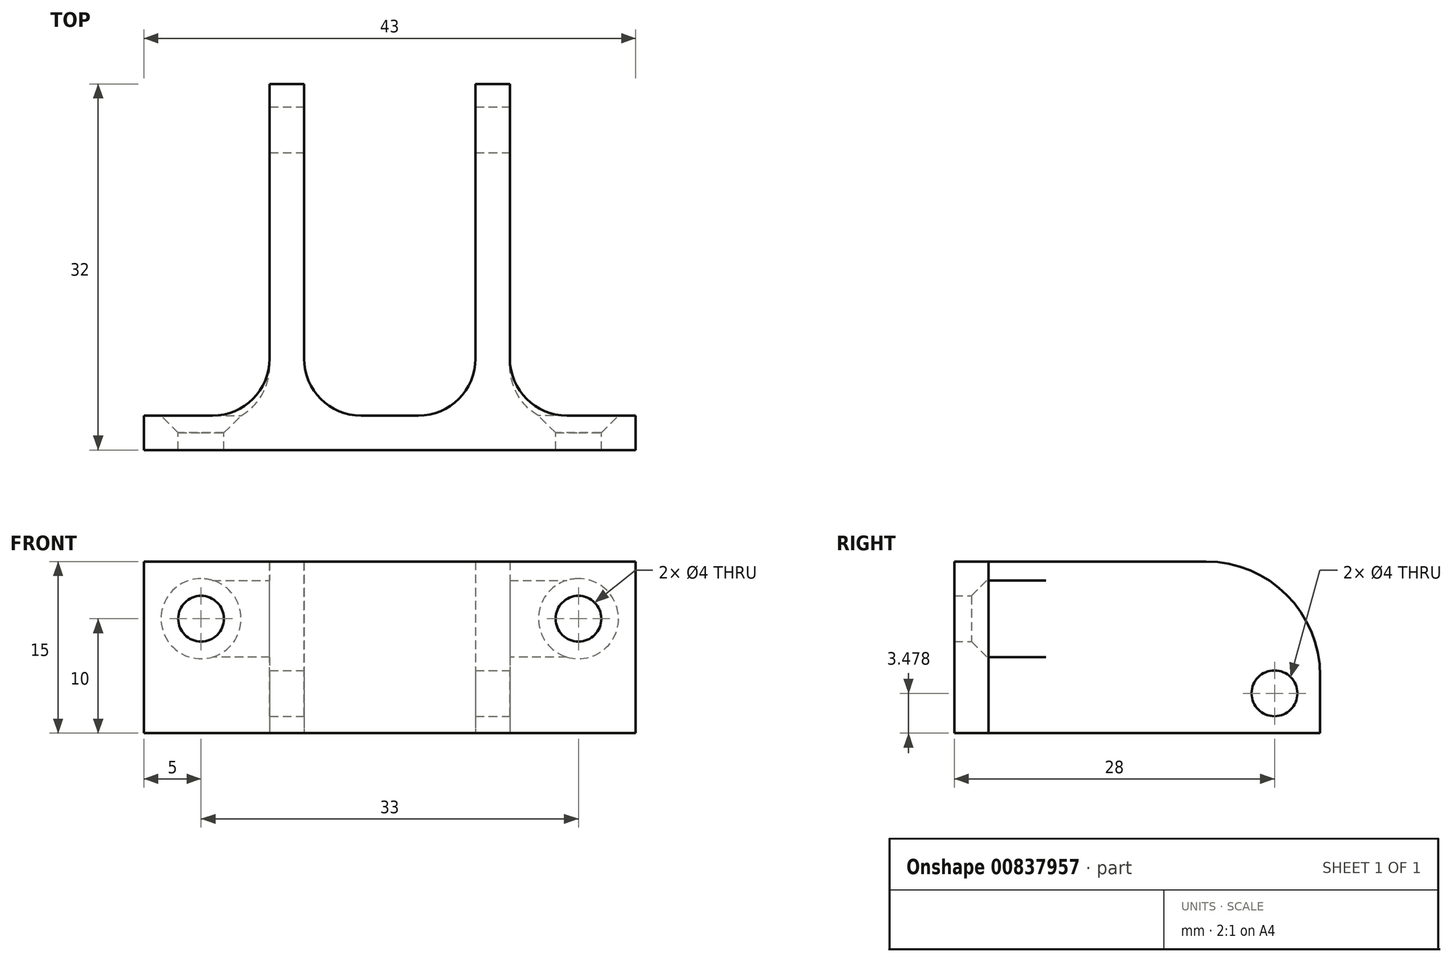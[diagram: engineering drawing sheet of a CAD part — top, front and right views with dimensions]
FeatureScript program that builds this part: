
annotation { "Feature Type Name" : "Feature", "Feature Type Description" : "" }
export const myFeature = defineFeature(function(context is Context, id is Id, definition is map)
    precondition{}
    {
        {
            var Q0;
            Q0=qCreatedBy(makeId("Top.planeOp"),FACE);
            var sketch = newSketch(context, id + "F0", { "sketchPlane" : qUnion([Q0])});
            skLineSegment(sketch, "E0", {"start": v(0, 29) * mm, "end": v(0, 0) * mm});
            skLineSegment(sketch, "E1", {"start": v(0, 0) * mm, "end": v(15, 0) * mm});
            skLineSegment(sketch, "E2", {"start": v(15, 0) * mm, "end": v(15, 29) * mm});
            skLineSegment(sketch, "E3", {"start": v(0, 0) * mm, "end": v(-14, 0) * mm});
            skLineSegment(sketch, "E4", {"start": v(15, 0) * mm, "end": v(29, 0) * mm});
            skLineSegment(sketch, "E5.0", {"start": v(18, -3) * mm, "end": v(18, 29) * mm});
            skLineSegment(sketch, "E5.1", {"start": v(-3, -3) * mm, "end": v(18, -3) * mm});
            skLineSegment(sketch, "E5.2", {"start": v(-3, 29) * mm, "end": v(-3, -3) * mm});
            skLineSegment(sketch, "E6", {"start": v(-3, -3) * mm, "end": v(-14, -3) * mm});
            skLineSegment(sketch, "E7", {"start": v(-14, -3) * mm, "end": v(-14, 0) * mm});
            skLineSegment(sketch, "E8", {"start": v(18, -3) * mm, "end": v(29, -3) * mm});
            skLineSegment(sketch, "E9", {"start": v(29, -3) * mm, "end": v(29, 0) * mm});
            skLineSegment(sketch, "E10", {"start": v(15, 29) * mm, "end": v(18, 29) * mm});
            skLineSegment(sketch, "E11", {"start": v(0, 29) * mm, "end": v(-3, 29) * mm});
            skSolve(sketch);
        }
        {
            var Q0;
            Q0 = qSketchRegion(id + "F0", true);
            extrude(context, id + "F1", {"entities" : qUnion([Q0]), "depth" : 15 * mm, "offsetDistance" : 25 * mm});
        }
        {
            var Q0;
            Q0=makeQuery(id+"F1.opExtrude","SWEPT_FACE",FACE,{"disambiguationData":[OSD([sQuery(id+"F0.wireOp",EDGE,"E5.0")])]});
            var sketch = newSketch(context, id + "F2", { "sketchPlane" : qUnion([Q0])});
            skLineSegment(sketch, "E12", {"start": v(25, 15) * mm, "end": v(25, 0) * mm, "construction": true});
            skLineSegment(sketch, "E13", {"start": v(28, 15) * mm, "end": v(28, 0) * mm, "construction": true});
            skCircle(sketch, "E14", {"center": v(25, 3.48) * mm, "radius": 2 * mm});
            skSolve(sketch);
        }
        {
            var Q0;
            Q0=makeQuery(id+"F2.imprint","IMPRINT",FACE,{"disambiguationData":[TD([[makeQuery(id+"F2.imprint","IMPRINT",EDGE,{"derivedFrom":sQuery(id+"F2.wireOp",EDGE,"E14")}),1.0]])]});
            var Q1;
            Q1=sQuery(id+"F2.wireOp",EDGE,"E14");
            extrude(context, id + "F3", {"entities" : qUnion([Q0]), "operationType" : NewBodyOperationType.REMOVE, "surfaceEntities" : qUnion([Q1]), "oppositeDirection" : true, "depth" : 25 * mm, "offsetDistance" : 25 * mm});
        }
        {
            var Q0;
            Q0=makeQuery(id+"F1.opExtrude","SWEPT_FACE",FACE,{"disambiguationData":[OSD([sQuery(id+"F0.wireOp",EDGE,"E4")])]});
            var sketch = newSketch(context, id + "F4", { "sketchPlane" : qUnion([Q0])});
            skLineSegment(sketch, "E15", {"start": v(-7.5, 0) * mm, "end": v(-7.5, 15.31) * mm, "construction": true});
            skLineSegment(sketch, "E16", {"start": v(13.84, 10) * mm, "end": v(-29, 10) * mm, "construction": true});
            skLineSegment(sketch, "E17", {"start": v(9, 0) * mm, "end": v(9, 15.42) * mm, "construction": true});
            skPoint(sketch, "E18", {"position": v(9, 10) * mm});
            skPoint(sketch, "E19", {"position": v(16.74, 5.7) * mm});
            skPoint(sketch, "E20.MirrorP", {"position": v(-24, 10) * mm});
            skSolve(sketch);
        }
        {
            var Q0;
            Q0=sQuery(id+"F4.wireOp",VERTEX,"E18");
            var Q1;
            Q1=sQuery(id+"F4.wireOp",VERTEX,"E20.MirrorP");
            var Q2;
            Q2=makeQuery(id+"F1.opExtrude","SWEPT_BODY",BODY,{"disambiguationData":[OSD([sQuery(id+"F0.wireOp",EDGE,"E0"),sQuery(id+"F0.wireOp",EDGE,"E1"),sQuery(id+"F0.wireOp",EDGE,"E2"),sQuery(id+"F0.wireOp",EDGE,"E3"),sQuery(id+"F0.wireOp",EDGE,"E4"),sQuery(id+"F0.wireOp",EDGE,"E5.0"),sQuery(id+"F0.wireOp",EDGE,"E5.1"),sQuery(id+"F0.wireOp",EDGE,"E5.2"),sQuery(id+"F0.wireOp",EDGE,"E6"),sQuery(id+"F0.wireOp",EDGE,"E7"),sQuery(id+"F0.wireOp",EDGE,"E8"),sQuery(id+"F0.wireOp",EDGE,"E9"),sQuery(id+"F0.wireOp",EDGE,"E10"),sQuery(id+"F0.wireOp",EDGE,"E11")])]});
            hole(context, id + "F5", {"style" : HoleStyle.C_SINK, "endStyle" : HoleEndStyle.THROUGH, "holeDiameter" : 4 * mm, "cSinkDiameter" : 7 * mm, "cSinkAngle" : 90 * degree, "majorDiameter" : 5 * mm, "isTappedThrough" : true, "tappedDepth" : 12 * mm, "tapClearance" : 3, "locations" : qUnion([Q0, Q1]), "scope" : qUnion([Q2])});
        }
        {
            var Q0;
            Q0=makeQuery(id+"F1.opExtrude","SWEPT_EDGE",EDGE,{"disambiguationData":[OSD([sQuery(id+"F0.wireOp",EDGE,"E0"),sQuery(id+"F0.wireOp",EDGE,"E1"),sQuery(id+"F0.wireOp",EDGE,"E3")])]});
            var Q1;
            Q1=makeQuery(id+"F1.opExtrude","SWEPT_EDGE",EDGE,{"disambiguationData":[OSD([sQuery(id+"F0.wireOp",EDGE,"E1"),sQuery(id+"F0.wireOp",EDGE,"E2"),sQuery(id+"F0.wireOp",EDGE,"E4")])]});
            var Q2;
            Q2=makeQuery(id+"F1.opExtrude","SWEPT_EDGE",EDGE,{"disambiguationData":[OSD([sQuery(id+"F0.wireOp",EDGE,"E3"),sQuery(id+"F0.wireOp",EDGE,"E5.2")])]});
            var Q3;
            Q3=makeQuery(id+"F1.opExtrude","SWEPT_EDGE",EDGE,{"disambiguationData":[OSD([sQuery(id+"F0.wireOp",EDGE,"E4"),sQuery(id+"F0.wireOp",EDGE,"E5.0")])]});
            fillet(context, id + "F6", {"entities" : qUnion([Q0, Q1, Q2, Q3]), "radius" : 5 * mm, "tangentPropagation" : true, "allowEdgeOverflow" : false});
        }
        {
            var Q0;
            Q0=makeQuery(id+"F1.opExtrude","CAP_EDGE",EDGE,{"disambiguationData":[OSD([sQuery(id+"F0.wireOp",EDGE,"E11")])],"isStart":false});
            var Q1;
            Q1=makeQuery(id+"F1.opExtrude","CAP_EDGE",EDGE,{"disambiguationData":[OSD([sQuery(id+"F0.wireOp",EDGE,"E10")])],"isStart":false});
            fillet(context, id + "F7", {"entities" : qUnion([Q0, Q1]), "radius" : 10 * mm, "tangentPropagation" : true, "allowEdgeOverflow" : false});
        }
    });
